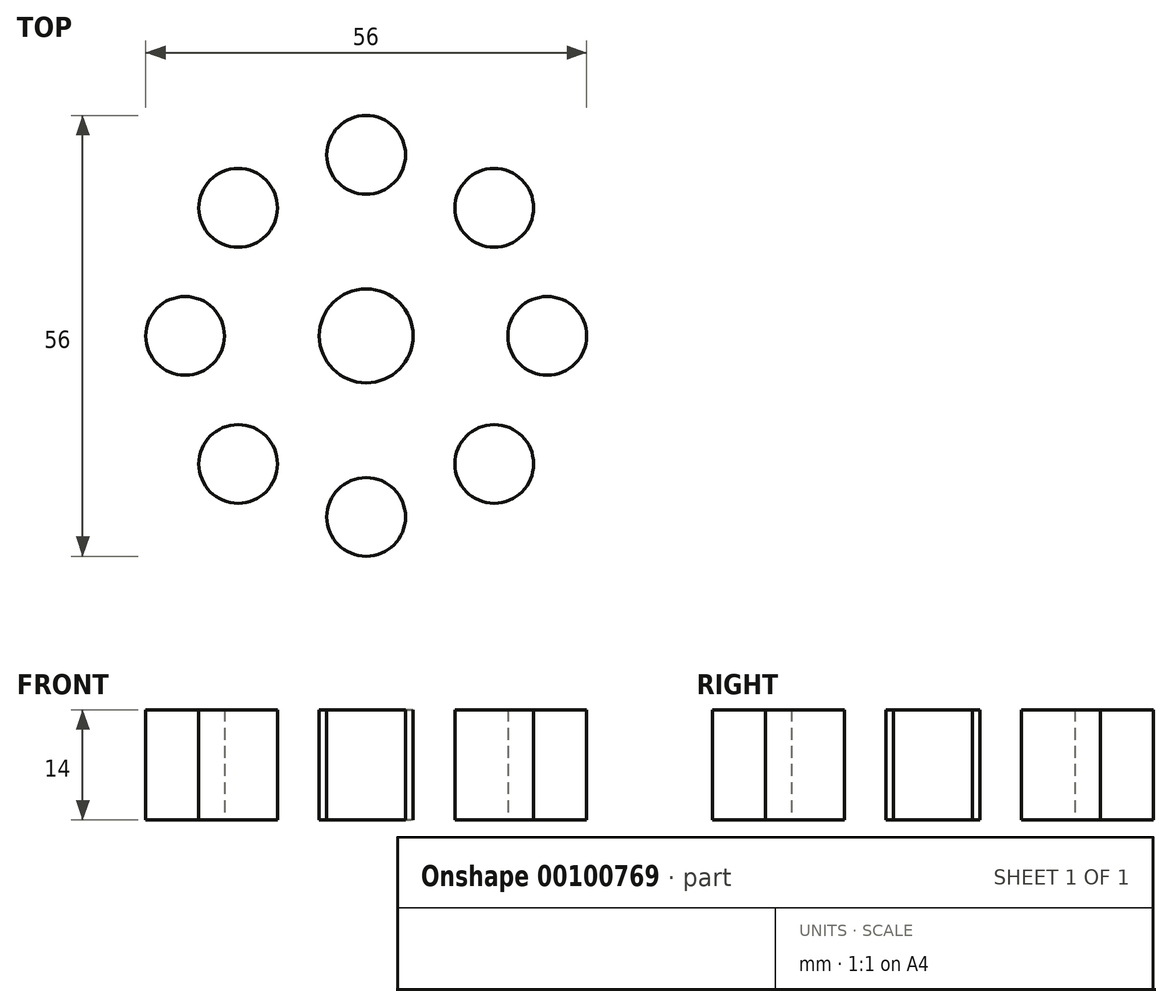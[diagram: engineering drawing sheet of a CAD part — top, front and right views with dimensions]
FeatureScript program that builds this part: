
annotation { "Feature Type Name" : "Feature", "Feature Type Description" : "" }
export const myFeature = defineFeature(function(context is Context, id is Id, definition is map)
    precondition{}
    {
        {
            var Q0;
            Q0=qCreatedBy(makeId("Top.planeOp"),FACE);
            var sketch = newSketch(context, id + "F0", { "sketchPlane" : qUnion([Q0])});
            skCircle(sketch, "E0", {"center": v(0, 0) * mm, "radius": 5.96 * mm});
            skCircle(sketch, "E1", {"center": v(0, 0) * mm, "radius": 18 * mm, "construction": true});
            skCircle(sketch, "E2", {"center": v(0, 0) * mm, "radius": 28 * mm, "construction": true});
            skLineSegment(sketch, "E3", {"start": v(0, 28) * mm, "end": v(0, 18) * mm, "construction": true});
            skCircle(sketch, "E4", {"center": v(0, 23) * mm, "radius": 5 * mm});
            skCircle(sketch, "E5.1.0", {"center": v(-16.26, 16.26) * mm, "radius": 5 * mm});
            skCircle(sketch, "E5.2.0", {"center": v(-23, 0) * mm, "radius": 5 * mm});
            skCircle(sketch, "E5.3.0", {"center": v(-16.26, -16.26) * mm, "radius": 5 * mm});
            skCircle(sketch, "E5.4.0", {"center": v(0, -23) * mm, "radius": 5 * mm});
            skCircle(sketch, "E5.5.0", {"center": v(16.26, -16.26) * mm, "radius": 5 * mm});
            skCircle(sketch, "E5.6.0", {"center": v(23, 0) * mm, "radius": 5 * mm});
            skCircle(sketch, "E5.7.0", {"center": v(16.26, 16.26) * mm, "radius": 5 * mm});
            skSolve(sketch);
        }
        {
            var Q0;
            Q0 = qSketchRegion(id + "F0", true);
            extrude(context, id + "F1", {"entities" : qUnion([Q0]), "depth" : 14 * mm});
        }
    });
